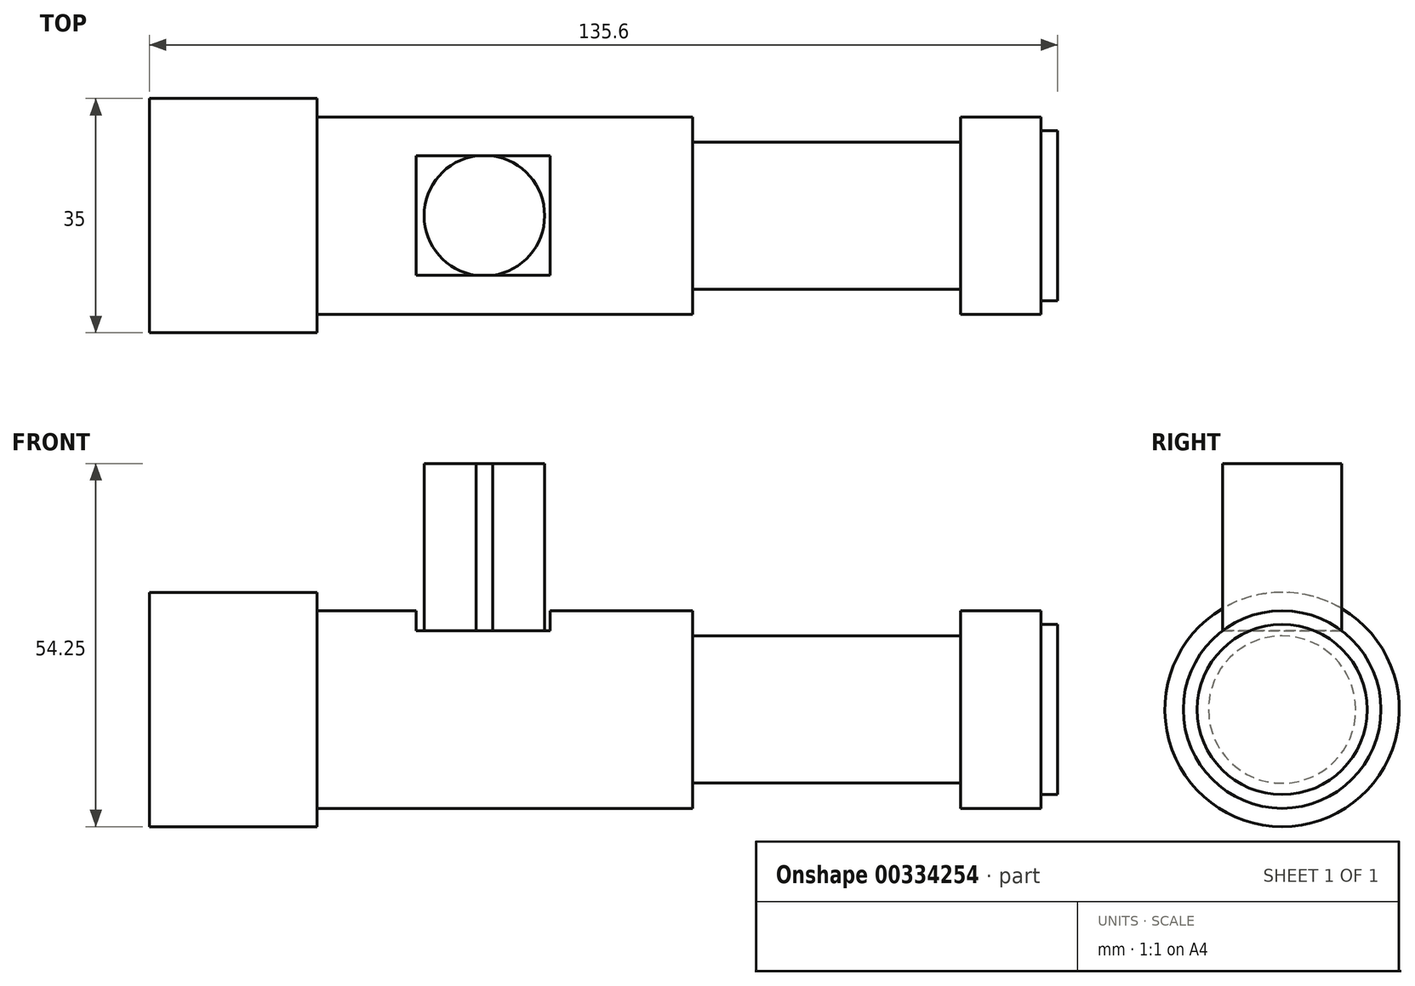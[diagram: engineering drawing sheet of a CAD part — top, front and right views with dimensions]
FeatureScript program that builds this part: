
annotation { "Feature Type Name" : "Feature", "Feature Type Description" : "" }
export const myFeature = defineFeature(function(context is Context, id is Id, definition is map)
    precondition{}
    {
        {
            var Q0;
            Q0=qCreatedBy(makeId("Front.planeOp"),FACE);
            var sketch = newSketch(context, id + "F0", { "sketchPlane" : qUnion([Q0])});
            skLineSegment(sketch, "E0", {"start": v(54.5, 0) * mm, "end": v(54.5, 12.7) * mm});
            skLineSegment(sketch, "E1", {"start": v(54.5, 12.7) * mm, "end": v(52, 12.7) * mm});
            skLineSegment(sketch, "E2", {"start": v(52, 12.7) * mm, "end": v(52, 14.75) * mm});
            skLineSegment(sketch, "E3", {"start": v(52, 14.75) * mm, "end": v(40, 14.75) * mm});
            skLineSegment(sketch, "E4", {"start": v(40, 14.75) * mm, "end": v(40, 11) * mm});
            skLineSegment(sketch, "E5", {"start": v(40, 11) * mm, "end": v(0, 11) * mm});
            skLineSegment(sketch, "E6", {"start": v(0, 11) * mm, "end": v(0, 14.75) * mm});
            skLineSegment(sketch, "E7", {"start": v(0, 14.75) * mm, "end": v(-56.1, 14.75) * mm});
            skLineSegment(sketch, "E8", {"start": v(-81.1, 17.5) * mm, "end": v(-81.1, 0) * mm});
            skLineSegment(sketch, "E9", {"start": v(-81.1, 17.5) * mm, "end": v(-56.1, 17.5) * mm});
            skLineSegment(sketch, "E10", {"start": v(-56.1, 17.5) * mm, "end": v(-56.1, 14.75) * mm});
            skLineSegment(sketch, "E11", {"start": v(82.05, 0) * mm, "end": v(-121.17, 0) * mm, "construction": true});
            skLineSegment(sketch, "E12", {"start": v(-81.1, 0) * mm, "end": v(54.5, 0) * mm});
            skSolve(sketch);
        }
        {
            var Q0;
            Q0=makeQuery(id+"F0.imprint","IMPRINT",FACE,{"disambiguationData":[TD([[makeQuery(id+"F0.imprint","IMPRINT",EDGE,{"derivedFrom":sQuery(id+"F0.wireOp",EDGE,"E0")}),1.0]])]});
            var Q1;
            Q1=sQuery(id+"F0.wireOp",EDGE,"E8");
            var Q2;
            Q2=sQuery(id+"F0.wireOp",EDGE,"E7");
            var Q3;
            Q3=sQuery(id+"F0.wireOp",EDGE,"E1");
            var Q4;
            Q4=sQuery(id+"F0.wireOp",EDGE,"E4");
            var Q5;
            Q5=sQuery(id+"F0.wireOp",EDGE,"E6");
            var Q6;
            Q6=sQuery(id+"F0.wireOp",EDGE,"E10");
            var Q7;
            Q7=sQuery(id+"F0.wireOp",EDGE,"E9");
            var Q8;
            Q8=sQuery(id+"F0.wireOp",EDGE,"E5");
            var Q9;
            Q9=sQuery(id+"F0.wireOp",EDGE,"E3");
            var Q10;
            Q10=sQuery(id+"F0.wireOp",EDGE,"E0");
            var Q11;
            Q11=sQuery(id+"F0.wireOp",EDGE,"E2");
            var Q12;
            Q12=sQuery(id+"F0.wireOp",EDGE,"E11");
            revolve(context, id + "F1", {"entities" : qUnion([Q0]), "surfaceEntities" : qUnion([Q1, Q2, Q3, Q4, Q5, Q6, Q7, Q8, Q9, Q10, Q11]), "axis" : qUnion([Q12]), "revolveType" : RevolveType.FULL, "oppositeDirection" : true});
        }
        {
            var Q0;
            Q0=qCreatedBy(makeId("Front.planeOp"),FACE);
            var sketch = newSketch(context, id + "F2", { "sketchPlane" : qUnion([Q0])});
            skLineSegment(sketch, "E13", {"start": v(-21.3, 14.75) * mm, "end": v(-21.3, 11.75) * mm});
            skLineSegment(sketch, "E14", {"start": v(-21.3, 11.75) * mm, "end": v(-41.3, 11.75) * mm});
            skLineSegment(sketch, "E15", {"start": v(-41.3, 11.75) * mm, "end": v(-41.3, 14.75) * mm});
            skPoint(sketch, "E16", {"position": v(-31.3, 11.75) * mm});
            skLineSegment(sketch, "E17", {"start": v(-21.3, 14.75) * mm, "end": v(-41.3, 14.75) * mm});
            skSolve(sketch);
        }
        {
            var Q0;
            Q0 = qSketchRegion(id + "F2", true);
            extrude(context, id + "F3", {"entities" : qUnion([Q0]), "operationType" : NewBodyOperationType.REMOVE, "endBound" : BoundingType.SYMMETRIC, "depth" : 20.2 * mm});
        }
        {
            var Q0;
            Q0=makeQuery(id+"F3.boolean.opBoolean","COPY",FACE,{"derivedFrom":makeQuery(id+"F3.opExtrude","SWEPT_FACE",FACE,{"disambiguationData":[OSD([sQuery(id+"F2.wireOp",EDGE,"E14")])]})});
            var sketch = newSketch(context, id + "F4", { "sketchPlane" : qUnion([Q0])});
            skCircle(sketch, "E18", {"center": v(-31.1, 0) * mm, "radius": 9 * mm});
            skPoint(sketch, "E19", {"position": v(-41.3, 0) * mm});
            skSolve(sketch);
        }
        {
            var Q0;
            {var subQ0=sQuery(id+"F4.wireOp",EDGE,"E18");var subQ1=makeQuery(id+"F3.opExtrude","SWEPT_FACE",FACE,{"disambiguationData":[OSD([sQuery(id+"F2.wireOp",EDGE,"E14")])]});var subQ2=makeQuery(id+"F1.opRevolve","SWEPT_FACE",FACE,{"disambiguationData":[OSD([sQuery(id+"F0.wireOp",EDGE,"E7")])]});var subQ3=makeQuery(id+"F3.boolean.opBoolean","INTERSECT",EDGE,{"disambiguationData":[OD(1.0)],"derivedFrom":[subQ2,subQ1]});var subQ4=makeQuery(id+"F4.imprint","INTERSECT",VERTEX,{"disambiguationData":[OD(0.0)],"derivedFrom":[subQ3,subQ0]});Q0=makeQuery(id+"F4.imprint","IMPRINT",FACE,{"disambiguationData":[TD([[makeQuery(id+"F4.imprint","IMPRINT",EDGE,{"disambiguationData":[TD([[subQ4,-1.0]])],"derivedFrom":subQ0}),1.0]])]});}
            var Q1;
            Q1=sQuery(id+"F4.wireOp",EDGE,"E18");
            extrude(context, id + "F5", {"entities" : qUnion([Q0]), "operationType" : NewBodyOperationType.ADD, "surfaceEntities" : qUnion([Q1]), "depth" : 25 * mm});
        }
    });
